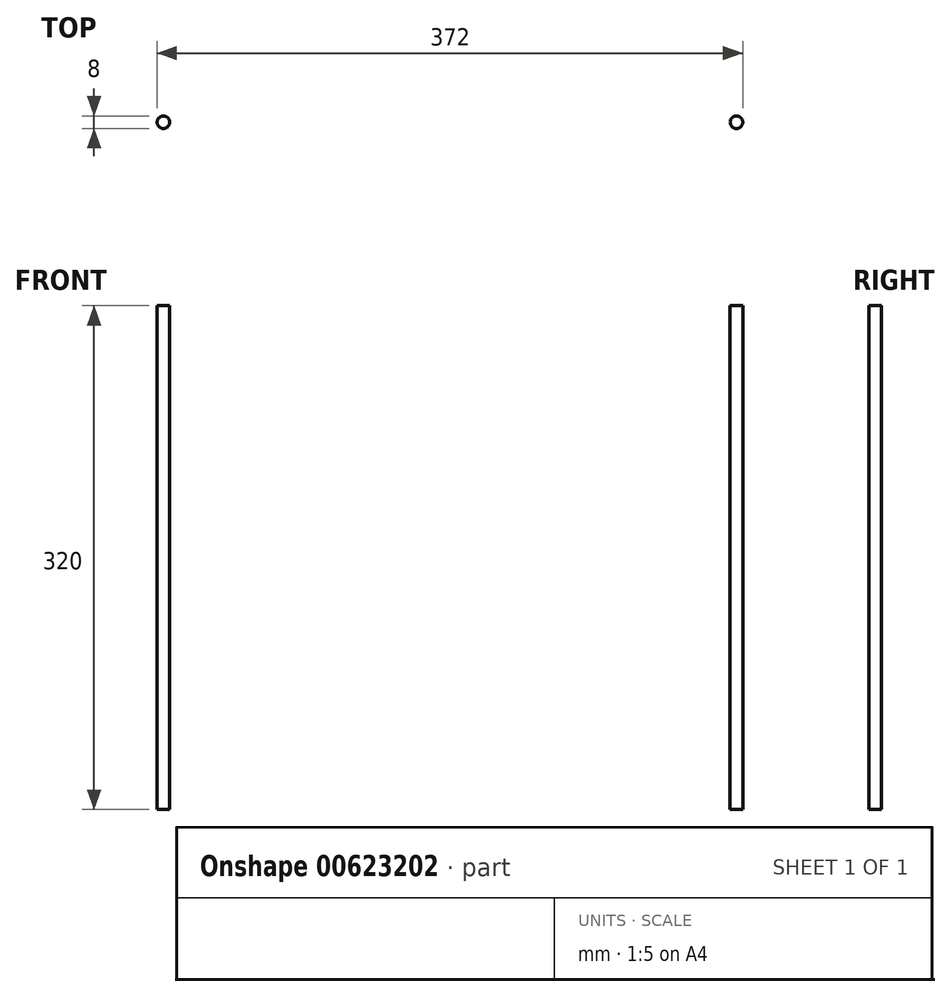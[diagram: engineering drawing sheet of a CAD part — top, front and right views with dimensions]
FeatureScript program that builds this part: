
annotation { "Feature Type Name" : "Feature", "Feature Type Description" : "" }
export const myFeature = defineFeature(function(context is Context, id is Id, definition is map)
    precondition{}
    {
        {
            var Q0;
            Q0=qCreatedBy(makeId("Top.planeOp"),FACE);
            var sketch = newSketch(context, id + "F0", { "sketchPlane" : qUnion([Q0])});
            skCircle(sketch, "E0", {"center": v(0, 0) * mm, "radius": 4 * mm});
            skCircle(sketch, "E1", {"center": v(-364, 0) * mm, "radius": 4 * mm});
            skSolve(sketch);
        }
        {
            var Q0;
            Q0=qSketchRegion(id+"F0",true);
            extrude(context, id + "F1", {"entities" : qUnion([Q0]), "oppositeDirection" : true, "depth" : 320 * mm, "offsetDistance" : 25 * mm});
        }
    });
